# Revit family: Hager-Panelboard_600A-800A_DIN_Rail_Extension_Boxes-syst-NoHosted-UK-en
name_source: partatom
category: Electrical Equipment
units: mm (PartAtom-declared; Revit-internal decimal feet)

## family parameters
Always vertical = Yes
Cut with Voids When Loaded = No
Panel Configuration = Two Columns, Circuits Across
Part Type = Panelboard
Room Calculation Point = No
Round Connector Dimension = Use Diameter
Shared = No
Work Plane-Based = Yes

## types (4) — shared parameters
Default Elevation = 1219 mm
EF000003 - Mounting method = EV000384 - Surface mounted (plaster)
EF000007 - Colour = EV000154 - Other
EF000008 - Width = 900 mm  [stored 2.95276 ft]
EF000049 - Depth = 220 mm  [stored 0.721785 ft]
EF000118 - With mounting plate = No
EF000339 - Type of cover = EV004216 - Door
EF001062 - EMC-version = No
EF001088 - Extension possible = No
EF001134 - DIN-rail = No
EF001596 - Material housing = EV000179 - Steel
EF002950 - Width in number of modular spacings = 34
EF004462 - Type of closure = EV001412 - Cylinder
EF005474 - Degree of protection (IP) = EV006414 - IP3X
EF006306 - With lock = Yes
EF015776 - Earthing terminal block = Yes
EF015777 - Neutral terminal block = Yes
EF015941 - Signal passing door = No
HG000001 - Number of columns = 1
HG000002 - With door or cover = Yes
HG000003 - Range = Panelboards
HG000005 - Thickness = 3 mm  [stored 0.00984252 ft]
HG000006 - Flush mounted = No
HG000009 - Double swing door = No
HG000010 - Asymmetric doors = No
HG000011 - Empty rows from bottom = No
HG000017 - Distance between poles = 18 mm  [stored 0.0590551 ft]
Manufacturer = Hager
Type Comments = Panelboards
zero-valued in all types: EF000218 - Built-in depth, EF000332 - Built-in height, EF000846 - Built-in width, EF001131 - Internal depth, HG000007 - Number of empty columns, HG000008 - Number of empty rows

## per-type parameters (varying)
| type | EF000040 - Height | EF000116 - RAL-number | EF000266 - Number of rows | EF006244 - Transparent cover/door | HG000004 - Manufacturer reference | Model |
| Surface mounted IP3X W900 H300 D220 34 Modular spacings - JF801E | 300 mm |  | 1 | No | JF801E | JF801E |
| Surface mounted IP3X W900 H300 D220 34 Modular spacings - JF801EG | 300 mm |  | 1 | Yes | JF801EG | JF801EG |
| Surface mounted IP3X W900 H450 D220 34 Modular spacings - JF803E | 450 mm  [stored 1.47638 ft] | 7035 | 2 | No | JF803E | JF803E |
| Surface mounted IP3X W900 H450 D220 34 Modular spacings - JF803EG | 450 mm  [stored 1.47638 ft] | 7035 | 2 | Yes | JF803EG | JF803EG |

note: [stored X ft] marks values corroborated as IEEE doubles in the binary element streams (Revit-internal decimal feet)

## geometry (parser evidence)
native form markers: Sweep x14
no freeform markers — native parametric forms only
